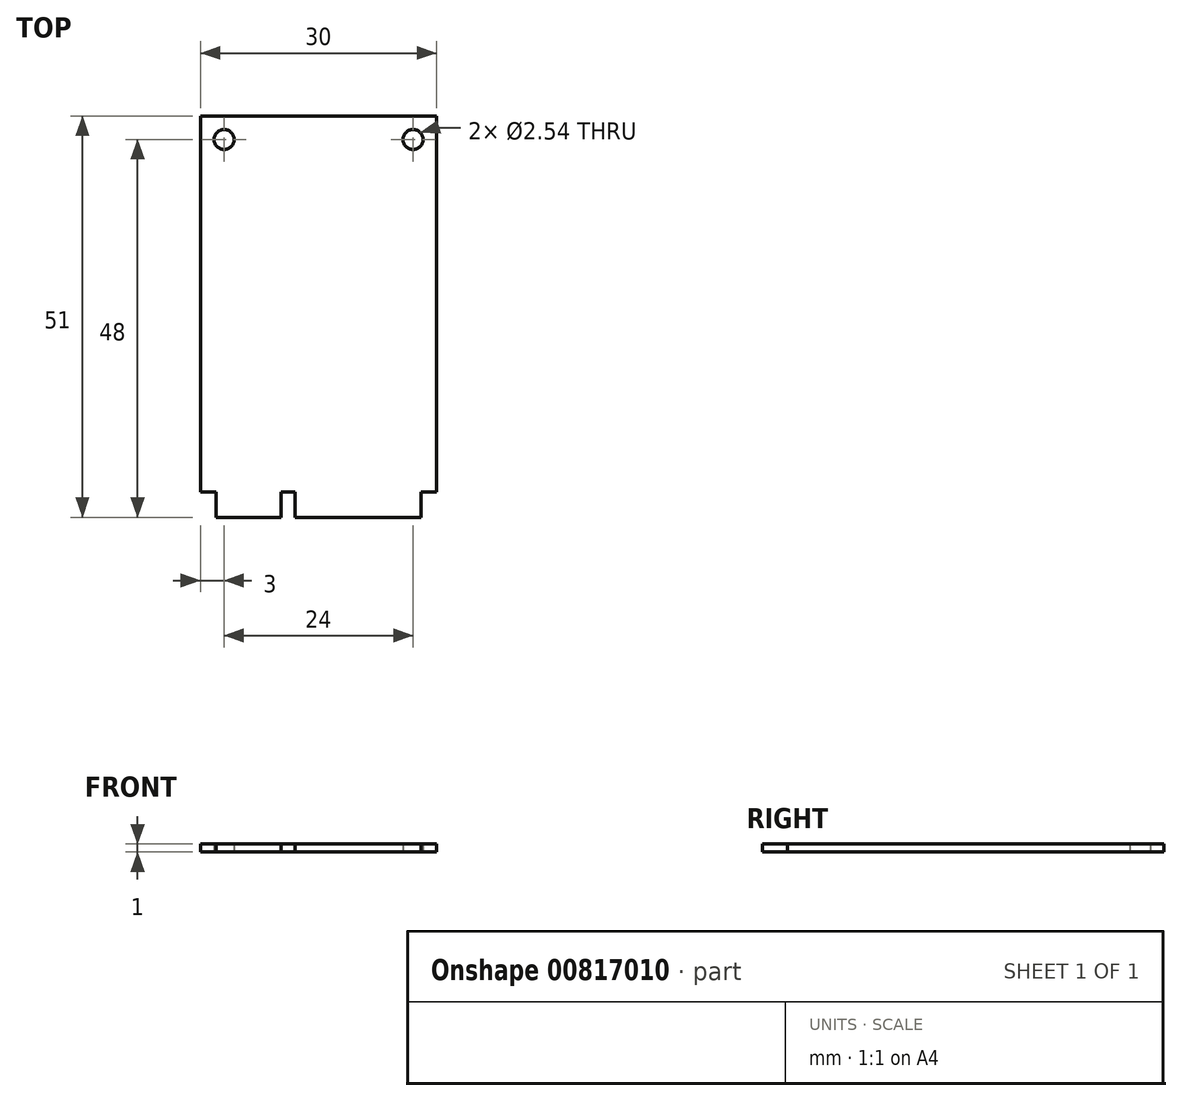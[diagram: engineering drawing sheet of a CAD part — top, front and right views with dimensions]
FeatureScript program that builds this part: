
annotation { "Feature Type Name" : "Feature", "Feature Type Description" : "" }
export const myFeature = defineFeature(function(context is Context, id is Id, definition is map)
    precondition{}
    {
        {
            var Q0;
            Q0=qCreatedBy(makeId("Top.planeOp"),FACE);
            var sketch = newSketch(context, id + "F0", { "sketchPlane" : qUnion([Q0])});
            skLineSegment(sketch, "E0.bottom", {"start": v(-15, 23.9) * mm, "end": v(15, 23.9) * mm});
            skLineSegment(sketch, "E0.top", {"start": v(-15, -23.9) * mm, "end": v(15, -23.9) * mm});
            skLineSegment(sketch, "E0.left", {"start": v(-15, 23.9) * mm, "end": v(-15, -23.9) * mm});
            skLineSegment(sketch, "E0.right", {"start": v(15, 23.9) * mm, "end": v(15, -23.9) * mm});
            skPoint(sketch, "E0.middle", {"position": v(0, 0) * mm});
            skLineSegment(sketch, "E1", {"start": v(-13, -23.9) * mm, "end": v(-13, -27.1) * mm});
            skLineSegment(sketch, "E2", {"start": v(-13, -27.1) * mm, "end": v(-4.75, -27.1) * mm});
            skLineSegment(sketch, "E3", {"start": v(-4.75, -27.1) * mm, "end": v(-4.75, -23.9) * mm});
            skLineSegment(sketch, "E4", {"start": v(-3, -23.9) * mm, "end": v(-3, -27.1) * mm});
            skLineSegment(sketch, "E5", {"start": v(-3, -27.1) * mm, "end": v(13, -27.1) * mm});
            skLineSegment(sketch, "E6", {"start": v(13, -27.1) * mm, "end": v(13, -23.9) * mm});
            skCircle(sketch, "E7", {"center": v(-12, 20.9) * mm, "radius": 1.27 * mm});
            skLineSegment(sketch, "E8", {"start": v(0, 0) * mm, "end": v(0, 23.9) * mm, "construction": true});
            skCircle(sketch, "E9.MirrorC", {"center": v(12, 20.9) * mm, "radius": 1.27 * mm});
            skSolve(sketch);
        }
        {
            var Q0;
            Q0=qSketchRegion(id+"F0",true);
            extrude(context, id + "F1", {"entities" : qUnion([Q0]), "depth" : 1 * mm});
        }
    });
